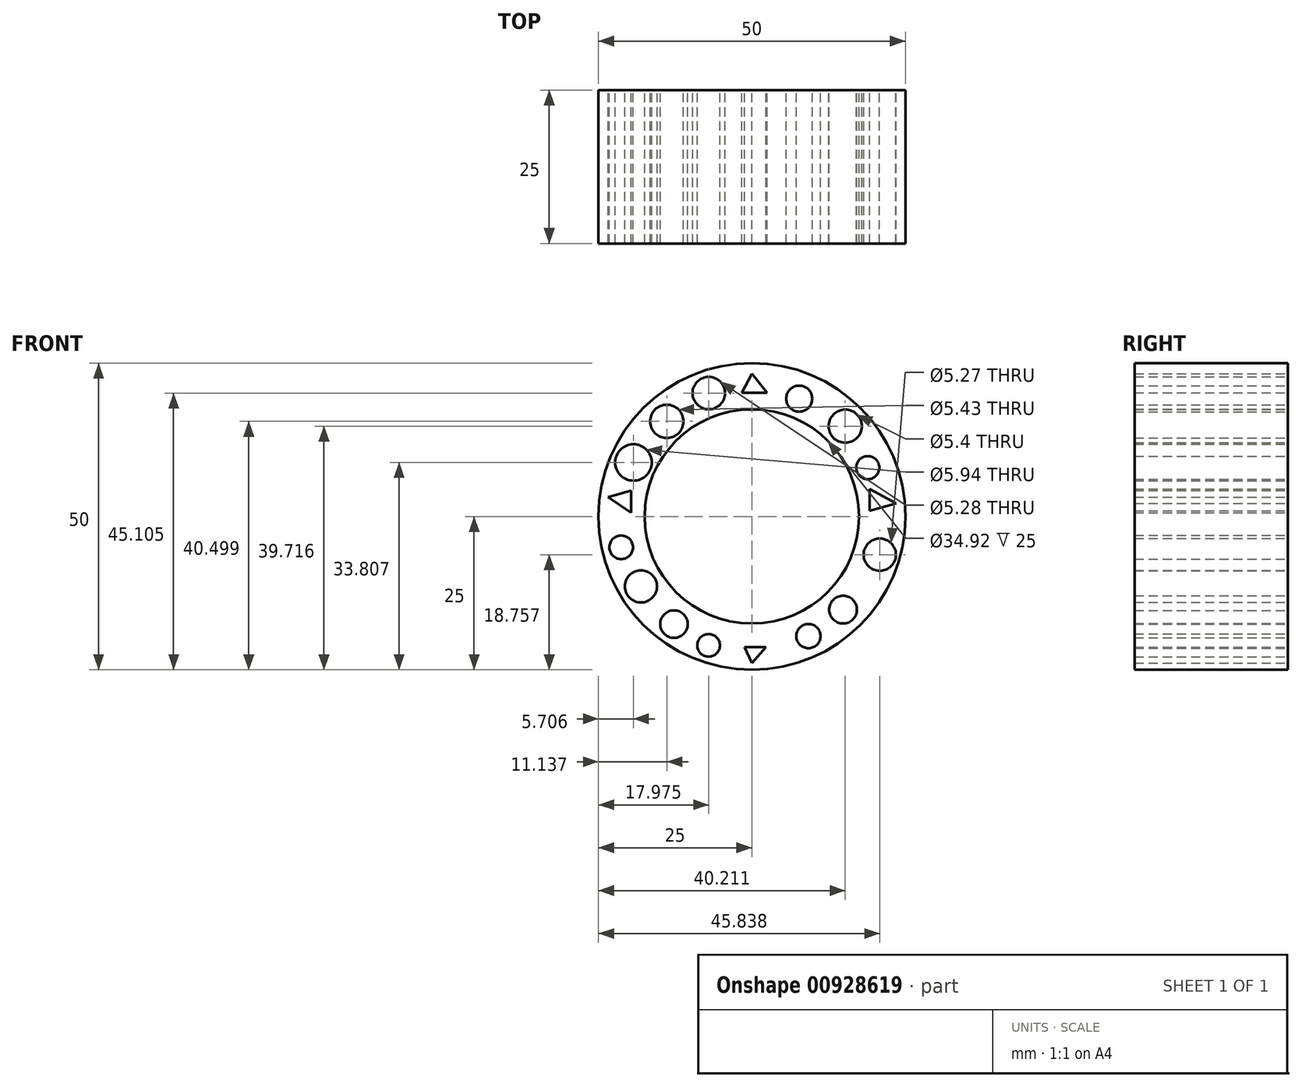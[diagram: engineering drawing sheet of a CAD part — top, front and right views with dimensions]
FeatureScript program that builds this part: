
annotation { "Feature Type Name" : "Feature", "Feature Type Description" : "" }
export const myFeature = defineFeature(function(context is Context, id is Id, definition is map)
    precondition{}
    {
        {
            var Q0;
            Q0=qCreatedBy(makeId("Front.planeOp"),FACE);
            var sketch = newSketch(context, id + "F0", { "sketchPlane" : qUnion([Q0])});
            skCircle(sketch, "E0", {"center": v(0, 0) * mm, "radius": 25 * mm});
            skCircle(sketch, "E1", {"center": v(0, 0) * mm, "radius": 17.46 * mm});
            skLineSegment(sketch, "E2", {"start": v(-2.62, 19.67) * mm, "end": v(3.98, 19.67) * mm});
            skLineSegment(sketch, "E3", {"start": v(3.98, 19.67) * mm, "end": v(0, 24.23) * mm});
            skLineSegment(sketch, "E4", {"start": v(0, 24.23) * mm, "end": v(-2.62, 19.67) * mm});
            skLineSegment(sketch, "E5", {"start": v(-2.62, -20.1) * mm, "end": v(4.27, -20.1) * mm});
            skLineSegment(sketch, "E6", {"start": v(4.27, -20.1) * mm, "end": v(0, -25) * mm});
            skLineSegment(sketch, "E7", {"start": v(0, -25) * mm, "end": v(-2.62, -20.1) * mm});
            skLineSegment(sketch, "E8", {"start": v(18.72, 0) * mm, "end": v(18.72, 5.22) * mm});
            skLineSegment(sketch, "E9", {"start": v(18.72, 5.22) * mm, "end": v(24.9, 2.14) * mm});
            skLineSegment(sketch, "E10", {"start": v(24.9, 2.14) * mm, "end": v(18.72, 0) * mm});
            skLineSegment(sketch, "E11", {"start": v(-18.91, -0.8) * mm, "end": v(-18.91, 5.22) * mm});
            skLineSegment(sketch, "E12", {"start": v(-18.91, 5.22) * mm, "end": v(-24.8, 3.18) * mm});
            skLineSegment(sketch, "E13", {"start": v(-24.8, 3.18) * mm, "end": v(-18.91, -0.8) * mm});
            skLineSegment(sketch, "E14", {"start": v(-1.62, 20.19) * mm, "end": v(2.5, 20.19) * mm});
            skLineSegment(sketch, "E15", {"start": v(2.5, 20.19) * mm, "end": v(0, 23.3) * mm});
            skLineSegment(sketch, "E16", {"start": v(0, 23.3) * mm, "end": v(-1.62, 20.19) * mm});
            skLineSegment(sketch, "E17", {"start": v(19.19, 0.9) * mm, "end": v(19.19, 4.5) * mm});
            skLineSegment(sketch, "E18", {"start": v(19.19, 4.5) * mm, "end": v(23.5, 2.14) * mm});
            skLineSegment(sketch, "E19", {"start": v(23.5, 2.14) * mm, "end": v(19.19, 0.9) * mm});
            skLineSegment(sketch, "E20", {"start": v(-1.22, -21.31) * mm, "end": v(2.27, -21.31) * mm});
            skLineSegment(sketch, "E21", {"start": v(2.27, -21.31) * mm, "end": v(0, -23.92) * mm});
            skLineSegment(sketch, "E22", {"start": v(0, -23.92) * mm, "end": v(-1.22, -21.31) * mm});
            skLineSegment(sketch, "E23", {"start": v(-19.7, 0.57) * mm, "end": v(-19.7, 4.24) * mm});
            skLineSegment(sketch, "E24", {"start": v(-19.7, 4.24) * mm, "end": v(-23.45, 3.14) * mm});
            skLineSegment(sketch, "E25", {"start": v(-23.45, 3.14) * mm, "end": v(-19.7, 0.57) * mm});
            skCircle(sketch, "E26", {"center": v(-21.3, -5.03) * mm, "radius": 2.74 * mm});
            skCircle(sketch, "E27", {"center": v(-21.3, -5.03) * mm, "radius": 1.92 * mm});
            skCircle(sketch, "E28", {"center": v(-18.08, -11.4) * mm, "radius": 3.58 * mm});
            skCircle(sketch, "E29", {"center": v(-18.08, -11.4) * mm, "radius": 2.62 * mm});
            skCircle(sketch, "E30", {"center": v(-12.7, -17.56) * mm, "radius": 3.48 * mm});
            skCircle(sketch, "E31", {"center": v(-12.7, -17.56) * mm, "radius": 2.24 * mm});
            skCircle(sketch, "E32", {"center": v(-19.3, 8.8) * mm, "radius": 3.74 * mm});
            skCircle(sketch, "E33", {"center": v(-19.3, 8.8) * mm, "radius": 2.97 * mm});
            skCircle(sketch, "E34", {"center": v(-13.86, 15.5) * mm, "radius": 3.56 * mm});
            skCircle(sketch, "E35", {"center": v(-13.86, 15.5) * mm, "radius": 2.72 * mm});
            skCircle(sketch, "E36", {"center": v(-7.03, 20.1) * mm, "radius": 3.63 * mm});
            skCircle(sketch, "E37", {"center": v(-7.03, 20.1) * mm, "radius": 2.64 * mm});
            skCircle(sketch, "E38", {"center": v(7.7, 19.2) * mm, "radius": 3.23 * mm});
            skCircle(sketch, "E39", {"center": v(7.7, 19.2) * mm, "radius": 2.12 * mm});
            skCircle(sketch, "E40", {"center": v(15.21, 14.72) * mm, "radius": 3.82 * mm});
            skCircle(sketch, "E41", {"center": v(15.21, 14.72) * mm, "radius": 2.7 * mm});
            skCircle(sketch, "E42", {"center": v(18.88, 7.95) * mm, "radius": 3.18 * mm});
            skCircle(sketch, "E43", {"center": v(18.88, 7.95) * mm, "radius": 1.88 * mm});
            skCircle(sketch, "E44", {"center": v(20.84, -6.24) * mm, "radius": 4.15 * mm});
            skCircle(sketch, "E45", {"center": v(20.84, -6.24) * mm, "radius": 2.64 * mm});
            skCircle(sketch, "E46", {"center": v(-7.05, -21.02) * mm, "radius": 2.83 * mm});
            skCircle(sketch, "E47", {"center": v(-7.05, -21.02) * mm, "radius": 1.85 * mm});
            skCircle(sketch, "E48", {"center": v(14.86, -15.2) * mm, "radius": 3.43 * mm});
            skCircle(sketch, "E49", {"center": v(14.86, -15.2) * mm, "radius": 2.26 * mm});
            skCircle(sketch, "E50", {"center": v(9.2, -19.52) * mm, "radius": 3.35 * mm});
            skCircle(sketch, "E51", {"center": v(9.2, -19.52) * mm, "radius": 1.97 * mm});
            skSolve(sketch);
        }
        {
            var Q0;
            Q0=makeQuery(id+"F0.imprint","IMPRINT",FACE,{"disambiguationData":[TD([[makeQuery(id+"F0.imprint","IMPRINT",EDGE,{"derivedFrom":sQuery(id+"F0.wireOp",EDGE,"E11")}),1.0]])]});
            var Q1;
            Q1=makeQuery(id+"F0.imprint","IMPRINT",FACE,{"disambiguationData":[TD([[makeQuery(id+"F0.imprint","IMPRINT",EDGE,{"derivedFrom":sQuery(id+"F0.wireOp",EDGE,"E1")}),-1.0]])]});
            var Q2;
            Q2=makeQuery(id+"F0.imprint","IMPRINT",FACE,{"disambiguationData":[TD([[makeQuery(id+"F0.imprint","IMPRINT",EDGE,{"derivedFrom":sQuery(id+"F0.wireOp",EDGE,"E5")}),-1.0]])]});
            var Q3;
            Q3=makeQuery(id+"F0.imprint","IMPRINT",FACE,{"disambiguationData":[TD([[makeQuery(id+"F0.imprint","IMPRINT",EDGE,{"derivedFrom":sQuery(id+"F0.wireOp",EDGE,"E8")}),-1.0]])]});
            var Q4;
            Q4=makeQuery(id+"F0.imprint","IMPRINT",FACE,{"disambiguationData":[TD([[makeQuery(id+"F0.imprint","IMPRINT",EDGE,{"derivedFrom":sQuery(id+"F0.wireOp",EDGE,"E2")}),1.0]])]});
            var Q5;
            {var subQ0=sQuery(id+"F0.wireOp",EDGE,"E13");Q5=makeQuery(id+"F0.imprint","IMPRINT",FACE,{"disambiguationData":[TD([[makeQuery(id+"F0.imprint","IMPRINT",EDGE,{"derivedFrom":subQ0}),1.0]])]});}
            var Q6;
            Q6=makeQuery(id+"F0.imprint","IMPRINT",FACE,{"disambiguationData":[TD([[makeQuery(id+"F0.imprint","IMPRINT",EDGE,{"derivedFrom":sQuery(id+"F0.wireOp",EDGE,"E28")}),1.0]])]});
            var Q7;
            Q7=makeQuery(id+"F0.imprint","IMPRINT",FACE,{"disambiguationData":[TD([[makeQuery(id+"F0.imprint","IMPRINT",EDGE,{"derivedFrom":sQuery(id+"F0.wireOp",EDGE,"E26")}),1.0]])]});
            var Q8;
            Q8=makeQuery(id+"F0.imprint","IMPRINT",FACE,{"disambiguationData":[TD([[makeQuery(id+"F0.imprint","IMPRINT",EDGE,{"derivedFrom":sQuery(id+"F0.wireOp",EDGE,"E31")}),-1.0]])]});
            var Q9;
            Q9=makeQuery(id+"F0.imprint","IMPRINT",FACE,{"disambiguationData":[TD([[makeQuery(id+"F0.imprint","IMPRINT",EDGE,{"derivedFrom":sQuery(id+"F0.wireOp",EDGE,"E46")}),1.0]])]});
            var Q10;
            Q10=makeQuery(id+"F0.imprint","IMPRINT",FACE,{"disambiguationData":[TD([[makeQuery(id+"F0.imprint","IMPRINT",EDGE,{"derivedFrom":sQuery(id+"F0.wireOp",EDGE,"E50")}),1.0]])]});
            var Q11;
            Q11=makeQuery(id+"F0.imprint","IMPRINT",FACE,{"disambiguationData":[TD([[makeQuery(id+"F0.imprint","IMPRINT",EDGE,{"derivedFrom":sQuery(id+"F0.wireOp",EDGE,"E48")}),1.0]])]});
            var Q12;
            Q12=makeQuery(id+"F0.imprint","IMPRINT",FACE,{"disambiguationData":[TD([[makeQuery(id+"F0.imprint","IMPRINT",EDGE,{"derivedFrom":sQuery(id+"F0.wireOp",EDGE,"E45")}),-1.0]])]});
            var Q13;
            {var subQ0=sQuery(id+"F0.wireOp",EDGE,"E10");Q13=makeQuery(id+"F0.imprint","IMPRINT",FACE,{"disambiguationData":[TD([[makeQuery(id+"F0.imprint","IMPRINT",EDGE,{"derivedFrom":subQ0}),-1.0]])]});}
            var Q14;
            Q14=makeQuery(id+"F0.imprint","IMPRINT",FACE,{"disambiguationData":[TD([[makeQuery(id+"F0.imprint","IMPRINT",EDGE,{"derivedFrom":sQuery(id+"F0.wireOp",EDGE,"E43")}),-1.0]])]});
            var Q15;
            Q15=makeQuery(id+"F0.imprint","IMPRINT",FACE,{"disambiguationData":[TD([[makeQuery(id+"F0.imprint","IMPRINT",EDGE,{"derivedFrom":sQuery(id+"F0.wireOp",EDGE,"E39")}),-1.0]])]});
            var Q16;
            Q16=makeQuery(id+"F0.imprint","IMPRINT",FACE,{"disambiguationData":[TD([[makeQuery(id+"F0.imprint","IMPRINT",EDGE,{"derivedFrom":sQuery(id+"F0.wireOp",EDGE,"E33")}),-1.0]])]});
            var Q17;
            Q17=makeQuery(id+"F0.imprint","IMPRINT",FACE,{"disambiguationData":[TD([[makeQuery(id+"F0.imprint","IMPRINT",EDGE,{"derivedFrom":sQuery(id+"F0.wireOp",EDGE,"E35")}),-1.0]])]});
            var Q18;
            Q18=makeQuery(id+"F0.imprint","IMPRINT",FACE,{"disambiguationData":[TD([[makeQuery(id+"F0.imprint","IMPRINT",EDGE,{"derivedFrom":sQuery(id+"F0.wireOp",EDGE,"E36")}),1.0]])]});
            var Q19;
            Q19=makeQuery(id+"F0.imprint","IMPRINT",FACE,{"disambiguationData":[TD([[makeQuery(id+"F0.imprint","IMPRINT",EDGE,{"derivedFrom":sQuery(id+"F0.wireOp",EDGE,"E41")}),-1.0]])]});
            extrude(context, id + "F1", {"entities" : qUnion([Q0, Q1, Q2, Q3, Q4, Q5, Q6, Q7, Q8, Q9, Q10, Q11, Q12, Q13, Q14, Q15, Q16, Q17, Q18, Q19]), "depth" : 25 * mm, "offsetDistance" : 25 * mm});
        }
    });
